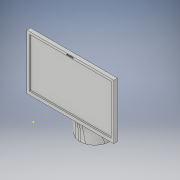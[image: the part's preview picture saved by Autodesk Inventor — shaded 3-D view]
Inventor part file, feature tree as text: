
AUTODESK INVENTOR PART (.ipt)
format: ipt  version: 2017 (Build 210142000, 142)  size: 397,824 bytes
history: native  units: in
note: dims shown in document units (in); Inventor stores cm internally (conversion verified against a paired STEP export)
features: sketch x10, fillet x7, extrude x5, plane x3, revolve x1, loft x1, emboss x1
ambient origin geometry x8: Origin, YZ Plane, XZ Plane, XY Plane, X Axis, Y Axis, Z Axis, Center Point
bodies: Solid1 (feature_tree)
feature tree (28):
  extrude  "Extrusion1"  Depth=12.0in
  extrude  "Extrusion2"  Depth=0.3in TaperAngle=0.0deg
  extrude  "Extrusion3"  Depth=2.1in
  fillet  "Fillet1"  [1 undecoded]
  revolve  "Revolution1"  [1 undecoded]
  plane  "Work Plane1"
  sketch  "Sketch5"  dims[d21=0.0in d22=90.0deg d23=0.0in d24=90.0deg]
  plane  "Work Plane2"
  sketch  "Sketch6"  dims[d25=0.1875in d26=0.0in d27=2.1in d28=0.1875in d29=0.0in]
  plane  "Work Plane4"
  loft  "Loft1"
  extrude  "Extrusion5"  Depth=2.1in
  fillet  "Fillet2"  Radius=0.1875in
  extrude  "Extrusion6"  Depth=0.02in
  fillet  "Fillet3"  Radius=0.1625in
  fillet  "Fillet4"  Radius=0.1625in
  fillet  "Fillet5"  Radius=0.1625in
  fillet  "Fillet6"  Radius=0.02in
  fillet  "Fillet7"  [1 undecoded]
  emboss  "Emboss1"
  sketch  "Sketch1"  dims[d0=19.0in d1=12.0in]
  sketch  "Sketch2"  dims[d2=0.8in d3=0.0in d5=0.3in d6=0.0in]
  sketch  "Sketch3"  dims[d9=2.1125in d10=0.0in d11=2.1in d12=180.0deg]
  sketch  "Sketch4"  dims[d17=5.5in d20=6.5in]
  sketch  "Sketch7"  dims[d30=0.1625in d31=0.1625in d32=0.1625in d33=0.1625in d34=0.1625in d37=0.02in d38=0.0in]
  sketch  "Sketch8"
  sketch  "Sketch9"
  sketch  "Sketch10"
note: 3 required parameter values undecoded (feature->parameter linkage not recoverable at this tier; creation-order binding heuristic only, values carry confidence <= 0.55)